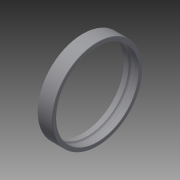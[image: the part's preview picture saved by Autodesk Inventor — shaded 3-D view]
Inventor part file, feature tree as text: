
AUTODESK INVENTOR PART (.ipt)
format: ipt  version: 2014 SP2 (Build 180246200, 246)  size: 148,480 bytes
history: native  units: mm
features: other x7, revolve x1, sketch x1
ambient origin geometry x8: Origin, YZ Plane, XZ Plane, XY Plane, X Axis, Y Axis, Z Axis, Center Point
bodies: Solid1 (feature_tree)
feature tree (9):
  revolve  "Revolution1"  [1 undecoded]
  other  "1_XY"
  other  "1_YZ"
  other  "1_ZX"
  other  "1_X"
  other  "1_Y"
  other  "1_Z"
  other  "1_Center"
  sketch  "Sketch_1"  dims[d0=360.0deg]
note: 1 required parameter value undecoded (feature->parameter linkage not recoverable at this tier; creation-order binding heuristic only, values carry confidence <= 0.55)
